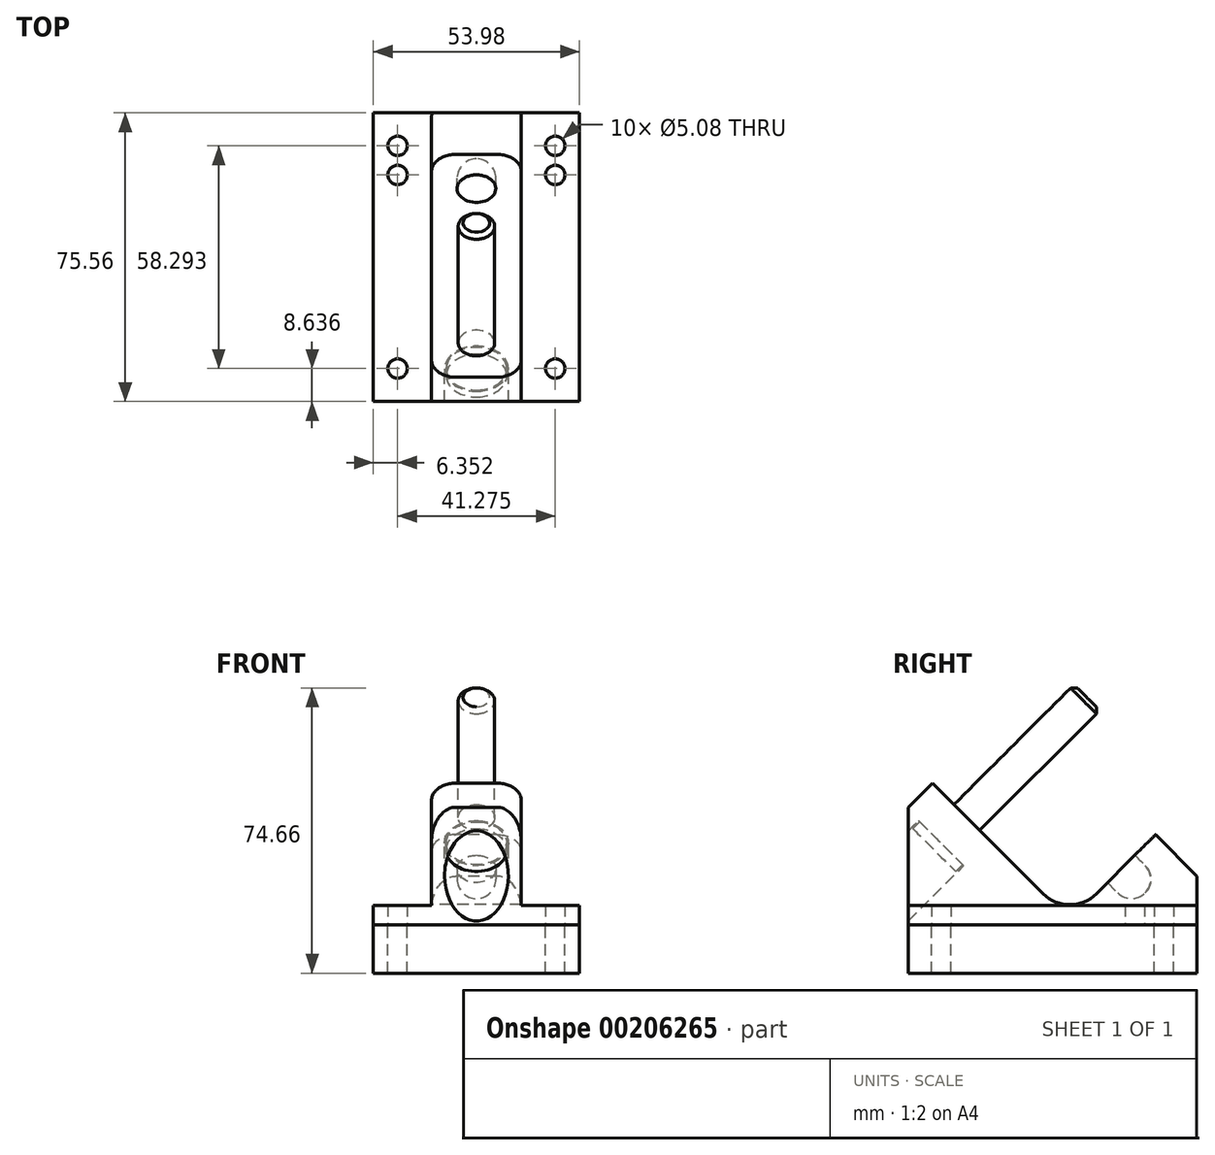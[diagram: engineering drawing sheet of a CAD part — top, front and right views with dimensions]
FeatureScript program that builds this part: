
annotation { "Feature Type Name" : "Feature", "Feature Type Description" : "" }
export const myFeature = defineFeature(function(context is Context, id is Id, definition is map)
    precondition{}
    {
        {
            var Q0;
            Q0=qCreatedBy(makeId("Right.planeOp"),FACE);
            var sketch = newSketch(context, id + "F0", { "sketchPlane" : qUnion([Q0])});
            skLineSegment(sketch, "E0", {"start": v(0, 0) * mm, "end": v(75.57, 0) * mm});
            skLineSegment(sketch, "E1", {"start": v(75.57, 0) * mm, "end": v(75.57, 12.7) * mm});
            skLineSegment(sketch, "E2", {"start": v(75.57, 12.7) * mm, "end": v(64.7, 23.57) * mm});
            skLineSegment(sketch, "E3", {"start": v(64.7, 23.57) * mm, "end": v(42.25, 1.12) * mm});
            skLineSegment(sketch, "E4", {"start": v(0, -14.12) * mm, "end": v(0, 0) * mm, "construction": true});
            skLineSegment(sketch, "E5", {"start": v(0, 0) * mm, "end": v(0, 30.72) * mm});
            skLineSegment(sketch, "E6", {"start": v(0, 30.72) * mm, "end": v(6.32, 37.04) * mm});
            skLineSegment(sketch, "E7", {"start": v(6.32, 37.04) * mm, "end": v(42.25, 1.12) * mm});
            skLineSegment(sketch, "E8", {"start": v(61.1, 19.98) * mm, "end": v(70.08, 11) * mm, "construction": true});
            skLineSegment(sketch, "E9", {"start": v(70.08, 11) * mm, "end": v(59.3, 0.22) * mm, "construction": true});
            skLineSegment(sketch, "E10", {"start": v(59.3, 0.22) * mm, "end": v(50.33, 9.2) * mm, "construction": true});
            skLineSegment(sketch, "E11", {"start": v(64.7, 5.6) * mm, "end": v(15.3, 55) * mm, "construction": true});
            skCircle(sketch, "E12", {"center": v(15.3, 55) * mm, "radius": 4 * mm, "construction": true});
            skLineSegment(sketch, "E13", {"start": v(15.3, 28.06) * mm, "end": v(28.77, 41.53) * mm, "construction": true});
            skCircle(sketch, "E14", {"center": v(58.4, 11.9) * mm, "radius": 5.08 * mm, "construction": true});
            skSolve(sketch);
        }
        {
            var Q0;
            Q0=qSketchRegion(id+"F0",true);
            extrude(context, id + "F1", {"entities" : qUnion([Q0]), "depth" : 26.99 * mm});
        }
        {
            var Q0;
            Q0=makeQuery(id+"F1.opExtrude","SWEPT_EDGE",EDGE,{"disambiguationData":[OSD([sQuery(id+"F0.wireOp",EDGE,"E3"),sQuery(id+"F0.wireOp",EDGE,"E7")])]});
            fillet(context, id + "F2", {"entities" : qUnion([Q0]), "radius" : 9.9 * mm, "tangentPropagation" : true, "allowEdgeOverflow" : false});
        }
        {
            var Q0;
            Q0=makeQuery(id+"F1.opExtrude","CAP_FACE",FACE,{"disambiguationData":[OSD([sQuery(id+"F0.wireOp",EDGE,"E0"),sQuery(id+"F0.wireOp",EDGE,"E1"),sQuery(id+"F0.wireOp",EDGE,"E2"),sQuery(id+"F0.wireOp",EDGE,"E3"),sQuery(id+"F0.wireOp",EDGE,"O8t1L6aE-7V4B-qQYz-aJHa-yxt4Uf4GNHZm"),sQuery(id+"F0.wireOp",EDGE,"dINw5n4X-CGaa-rPGi-QK1T-MrZfrRMsY7ox"),sQuery(id+"F0.wireOp",EDGE,"k2Hi1M4v-dZXO-cidX-ee3S-7WINr6mVTnzP")])],"isStart":false});
            var sketch = newSketch(context, id + "F3", { "sketchPlane" : qUnion([Q0])});
            skLineSegment(sketch, "E15.bottom", {"start": v(75.57, 5.08) * mm, "end": v(0, 5.08) * mm});
            skLineSegment(sketch, "E15.top", {"start": v(75.57, 37.04) * mm, "end": v(0, 37.04) * mm});
            skLineSegment(sketch, "E15.left", {"start": v(75.57, 5.08) * mm, "end": v(75.57, 37.04) * mm});
            skLineSegment(sketch, "E15.right", {"start": v(0, 5.08) * mm, "end": v(0, 37.04) * mm});
            skSolve(sketch);
        }
        {
            var Q0;
            Q0=qSketchRegion(id+"F3",true);
            extrude(context, id + "F4", {"entities" : qUnion([Q0]), "operationType" : NewBodyOperationType.REMOVE, "oppositeDirection" : true, "depth" : 15.24 * mm});
        }
        {
            var Q0;
            Q0=makeQuery(id+"F1.opExtrude","SWEPT_FACE",FACE,{"disambiguationData":[OSD([sQuery(id+"F0.wireOp",EDGE,"E0")])]});
            var sketch = newSketch(context, id + "F5", { "sketchPlane" : qUnion([Q0])});
            skLineSegment(sketch, "E16", {"start": v(20.64, -8.64) * mm, "end": v(20.64, -59.3) * mm, "construction": true});
            skLineSegment(sketch, "E17", {"start": v(20.64, -59.3) * mm, "end": v(20.64, -66.93) * mm, "construction": true});
            skCircle(sketch, "E18", {"center": v(20.64, -8.64) * mm, "radius": 2.54 * mm});
            skCircle(sketch, "E19", {"center": v(20.64, -59.3) * mm, "radius": 2.54 * mm});
            skCircle(sketch, "E20", {"center": v(20.64, -66.93) * mm, "radius": 2.54 * mm});
            skSolve(sketch);
        }
        {
            var Q0;
            Q0=qSketchRegion(id+"F5",true);
            extrude(context, id + "F6", {"entities" : qUnion([Q0]), "operationType" : NewBodyOperationType.REMOVE, "endBound" : BoundingType.UP_TO_NEXT, "oppositeDirection" : true, "depth" : 25.4 * mm});
        }
        {
            var Q0;
            Q0=makeQuery(id+"F1.opExtrude","CAP_FACE",FACE,{"disambiguationData":[OSD([sQuery(id+"F0.wireOp",EDGE,"E0"),sQuery(id+"F0.wireOp",EDGE,"E1"),sQuery(id+"F0.wireOp",EDGE,"E2"),sQuery(id+"F0.wireOp",EDGE,"E3"),sQuery(id+"F0.wireOp",EDGE,"O8t1L6aE-7V4B-qQYz-aJHa-yxt4Uf4GNHZm"),sQuery(id+"F0.wireOp",EDGE,"dINw5n4X-CGaa-rPGi-QK1T-MrZfrRMsY7ox"),sQuery(id+"F0.wireOp",EDGE,"k2Hi1M4v-dZXO-cidX-ee3S-7WINr6mVTnzP")])],"isStart":true});
            var sketch = newSketch(context, id + "F7", { "sketchPlane" : qUnion([Q0])});
            skLineSegment(sketch, "E21", {"start": v(-11.94, 31.43) * mm, "end": v(-5.2, 24.7) * mm});
            skLineSegment(sketch, "E22", {"start": v(-5.2, 24.7) * mm, "end": v(-2.67, 27.22) * mm});
            skLineSegment(sketch, "E23", {"start": v(-2.67, 27.22) * mm, "end": v(12.28, 12.28) * mm});
            skLineSegment(sketch, "E24", {"start": v(12.28, 12.28) * mm, "end": v(6.38, 6.38) * mm});
            skLineSegment(sketch, "E25", {"start": v(6.38, 6.38) * mm, "end": v(-15.3, 28.06) * mm});
            skLineSegment(sketch, "E26", {"start": v(-15.3, 28.06) * mm, "end": v(-16.61, 29.37) * mm, "construction": true});
            skLineSegment(sketch, "E27", {"start": v(-15.3, 28.06) * mm, "end": v(-11.94, 31.43) * mm});
            skLineSegment(sketch, "E28", {"start": v(0, 0) * mm, "end": v(6.38, 6.38) * mm});
            skSolve(sketch);
        }
        {
            var Q0;
            Q0=qSketchRegion(id+"F7",true);
            var Q1;
            Q1=sQuery(id+"F7.wireOp",EDGE,"E25");
            revolve(context, id + "F8", {"operationType" : NewBodyOperationType.REMOVE, "entities" : qUnion([Q0]), "axis" : qUnion([Q1]), "revolveType" : RevolveType.FULL, "oppositeDirection" : true});
        }
        {
            var Q0;
            Q0=qCreatedBy(makeId("Right.planeOp"),FACE);
            var sketch = newSketch(context, id + "F9", { "sketchPlane" : qUnion([Q0])});
            skLineSegment(sketch, "E29", {"start": v(2.96, 26.94) * mm, "end": v(5.2, 24.7) * mm});
            skLineSegment(sketch, "E30", {"start": v(5.2, 24.7) * mm, "end": v(43.37, 62.86) * mm});
            skLineSegment(sketch, "E31", {"start": v(43.37, 62.86) * mm, "end": v(46.74, 59.5) * mm});
            skLineSegment(sketch, "E32", {"start": v(46.74, 59.5) * mm, "end": v(6.77, 19.53) * mm});
            skLineSegment(sketch, "E33", {"start": v(6.77, 19.53) * mm, "end": v(1.16, 25.14) * mm});
            skLineSegment(sketch, "E34", {"start": v(1.16, 25.14) * mm, "end": v(2.96, 26.94) * mm});
            skLineSegment(sketch, "E35", {"start": v(6.77, 19.53) * mm, "end": v(2.3, 15.06) * mm, "construction": true});
            skPoint(sketch, "E36", {"position": v(8.78, 21.53) * mm});
            skSolve(sketch);
        }
        {
            var Q0;
            Q0=qSketchRegion(id+"F9",true);
            var Q1;
            Q1=sQuery(id+"F9.wireOp",EDGE,"E32");
            revolve(context, id + "F10", {"entities" : qUnion([Q0]), "axis" : qUnion([Q1]), "revolveType" : RevolveType.FULL});
        }
        {
            var Q0;
            Q0=makeQuery(id+"F4.boolean.opBoolean","INTERSECT",EDGE,{"derivedFrom":[makeQuery(id+"F1.opExtrude","SWEPT_FACE",FACE,{"disambiguationData":[OSD([sQuery(id+"F0.wireOp",EDGE,"E2")])]}),makeQuery(id+"F4.opExtrude","CAP_FACE",FACE,{"disambiguationData":[OSD([sQuery(id+"F3.wireOp",EDGE,"E15.bottom"),sQuery(id+"F3.wireOp",EDGE,"E15.top"),sQuery(id+"F3.wireOp",EDGE,"E15.left"),sQuery(id+"F3.wireOp",EDGE,"E15.right")])],"isStart":false})]});
            var Q1;
            Q1=makeQuery(id+"FPWNDdPn0RB2iZ7_1.opPattern","COPY",EDGE,{"derivedFrom":makeQuery(id+"F4.boolean.opBoolean","INTERSECT",EDGE,{"derivedFrom":[makeQuery(id+"F1.opExtrude","SWEPT_FACE",FACE,{"disambiguationData":[OSD([sQuery(id+"F0.wireOp",EDGE,"E2")])]}),makeQuery(id+"F4.opExtrude","CAP_FACE",FACE,{"disambiguationData":[OSD([sQuery(id+"F3.wireOp",EDGE,"E15.bottom"),sQuery(id+"F3.wireOp",EDGE,"E15.top"),sQuery(id+"F3.wireOp",EDGE,"E15.left"),sQuery(id+"F3.wireOp",EDGE,"E15.right")])],"isStart":false})]}),"instanceName":"1"});
            var Q2;
            Q2=makeQuery(id+"F4.boolean.opBoolean","INTERSECT",EDGE,{"derivedFrom":[makeQuery(id+"F1.opExtrude","SWEPT_FACE",FACE,{"disambiguationData":[OSD([sQuery(id+"F0.wireOp",EDGE,"E6")])]}),makeQuery(id+"F4.opExtrude","CAP_FACE",FACE,{"disambiguationData":[OSD([sQuery(id+"F3.wireOp",EDGE,"E15.bottom"),sQuery(id+"F3.wireOp",EDGE,"E15.top"),sQuery(id+"F3.wireOp",EDGE,"E15.left"),sQuery(id+"F3.wireOp",EDGE,"E15.right")])],"isStart":false})]});
            var Q3;
            Q3=makeQuery(id+"FPWNDdPn0RB2iZ7_1.opPattern","COPY",EDGE,{"derivedFrom":makeQuery(id+"F4.boolean.opBoolean","INTERSECT",EDGE,{"derivedFrom":[makeQuery(id+"F1.opExtrude","SWEPT_FACE",FACE,{"disambiguationData":[OSD([sQuery(id+"F0.wireOp",EDGE,"E6")])]}),makeQuery(id+"F4.opExtrude","CAP_FACE",FACE,{"disambiguationData":[OSD([sQuery(id+"F3.wireOp",EDGE,"E15.bottom"),sQuery(id+"F3.wireOp",EDGE,"E15.top"),sQuery(id+"F3.wireOp",EDGE,"E15.left"),sQuery(id+"F3.wireOp",EDGE,"E15.right")])],"isStart":false})]}),"instanceName":"1"});
            fillet(context, id + "F11", {"entities" : qUnion([Q0, Q1, Q2, Q3]), "radius" : 6.35 * mm, "tangentPropagation" : true, "allowEdgeOverflow" : false});
        }
        {
            var Q0;
            Q0=qCreatedBy(makeId("Right.planeOp"),FACE);
            var sketch = newSketch(context, id + "F12", { "sketchPlane" : qUnion([Q0])});
            skLineSegment(sketch, "E37.0", {"start": v(61.1, 19.98) * mm, "end": v(70.08, 11) * mm});
            skLineSegment(sketch, "E37.1", {"start": v(70.08, 11) * mm, "end": v(64.7, 5.6) * mm});
            skLineSegment(sketch, "E37.2", {"start": v(64.7, 5.6) * mm, "end": v(55.72, 14.59) * mm});
            skLineSegment(sketch, "E38", {"start": v(61.1, 19.98) * mm, "end": v(55.72, 14.59) * mm});
            skPoint(sketch, "E39.orphan", {"position": v(15.3, 55) * mm});
            skPoint(sketch, "E40.orphan", {"position": v(59.3, 0.22) * mm});
            skSolve(sketch);
        }
        {
            var Q0;
            Q0=qSketchRegion(id+"F12",true);
            var Q1;
            Q1=sQuery(id+"F12.wireOp",EDGE,"E37.2");
            revolve(context, id + "F13", {"operationType" : NewBodyOperationType.REMOVE, "entities" : qUnion([Q0]), "axis" : qUnion([Q1]), "revolveType" : RevolveType.FULL, "oppositeDirection" : true});
        }
        {
            var Q0;
            Q0=qCreatedBy(makeId("Right.planeOp"),FACE);
            var sketch = newSketch(context, id + "F14", { "sketchPlane" : qUnion([Q0])});
            skLineSegment(sketch, "E41.0", {"start": v(61.1, 19.98) * mm, "end": v(70.08, 11) * mm});
            skLineSegment(sketch, "E41.1", {"start": v(70.08, 11) * mm, "end": v(64.7, 5.6) * mm});
            skLineSegment(sketch, "E41.2", {"start": v(64.7, 5.6) * mm, "end": v(62, 8.3) * mm});
            skArc(sketch, "E41.3", {"start": v(62, 8.3) * mm, "mid": v(63.49, 11.9) * mm, "end": v(62, 15.49) * mm});
            skLineSegment(sketch, "E42", {"start": v(62, 15.49) * mm, "end": v(59.3, 18.18) * mm});
            skLineSegment(sketch, "E43", {"start": v(59.3, 18.18) * mm, "end": v(61.1, 19.98) * mm});
            skPoint(sketch, "E44.orphan", {"position": v(15.3, 55) * mm});
            skPoint(sketch, "E45.orphan", {"position": v(59.3, 0.22) * mm});
            skSolve(sketch);
        }
        {
            var Q0;
            Q0=qSketchRegion(id+"F14",true);
            var Q1;
            Q1=sQuery(id+"F0.wireOp",EDGE,"E11");
            revolve(context, id + "F15", {"entities" : qUnion([Q0]), "axis" : qUnion([Q1]), "revolveType" : RevolveType.FULL});
        }
        {
            var Q0;
            Q0=makeQuery(id+"F1.opExtrude","SWEPT_BODY",BODY,{"disambiguationData":[OSD([sQuery(id+"F0.wireOp",EDGE,"E0"),sQuery(id+"F0.wireOp",EDGE,"E1"),sQuery(id+"F0.wireOp",EDGE,"E2"),sQuery(id+"F0.wireOp",EDGE,"E3"),sQuery(id+"F0.wireOp",EDGE,"E5"),sQuery(id+"F0.wireOp",EDGE,"E6"),sQuery(id+"F0.wireOp",EDGE,"E7")])]});
            var Q1;
            Q1=qCreatedBy(makeId("Right.planeOp"),FACE);
            mirror(context, id + "F16", {"operationType" : NewBodyOperationType.ADD, "entities" : qUnion([Q0]), "mirrorPlane" : qUnion([Q1])});
        }
        {
            var Q0;
            Q0=makeQuery(id+"F10.opRevolve","SWEPT_EDGE",EDGE,{"disambiguationData":[OSD([sQuery(id+"F9.wireOp",EDGE,"E30"),sQuery(id+"F9.wireOp",EDGE,"E31")])]});
            chamfer(context, id + "F17", {"entities" : qUnion([Q0]), "width" : 1.27 * mm, "tangentPropagation" : true});
        }
        {
            var Q0;
            {var subQ0=makeQuery(id+"F1.opExtrude","SWEPT_FACE",FACE,{"disambiguationData":[OSD([sQuery(id+"F0.wireOp",EDGE,"E0")])]});Q0=makeQuery(id+"F16.boolean.opBoolean","MERGE",FACE,{"derivedFrom":[subQ0,makeQuery(id+"F16.opPattern","COPY",FACE,{"derivedFrom":subQ0,"instanceName":"1"})]});}
            var sketch = newSketch(context, id + "F18", { "sketchPlane" : qUnion([Q0])});
            skLineSegment(sketch, "E46.0", {"start": v(26.99, 0) * mm, "end": v(-26.99, 0) * mm});
            skLineSegment(sketch, "E46.1", {"start": v(26.99, 0) * mm, "end": v(26.99, -75.57) * mm});
            skLineSegment(sketch, "E46.2", {"start": v(26.99, -75.57) * mm, "end": v(-26.99, -75.57) * mm});
            skLineSegment(sketch, "E46.3", {"start": v(-26.99, 0) * mm, "end": v(-26.99, -75.57) * mm});
            skCircle(sketch, "E46.4", {"center": v(-20.64, -66.93) * mm, "radius": 2.54 * mm});
            skCircle(sketch, "E46.5", {"center": v(20.64, -66.93) * mm, "radius": 2.54 * mm});
            skCircle(sketch, "E46.6", {"center": v(20.64, -8.64) * mm, "radius": 2.54 * mm});
            skCircle(sketch, "E46.7", {"center": v(-20.64, -8.64) * mm, "radius": 2.54 * mm});
            skSolve(sketch);
        }
        {
            var Q0;
            Q0=qSketchRegion(id+"F18",true);
            extrude(context, id + "F19", {"entities" : qUnion([Q0]), "depth" : 12.7 * mm});
        }
    });
